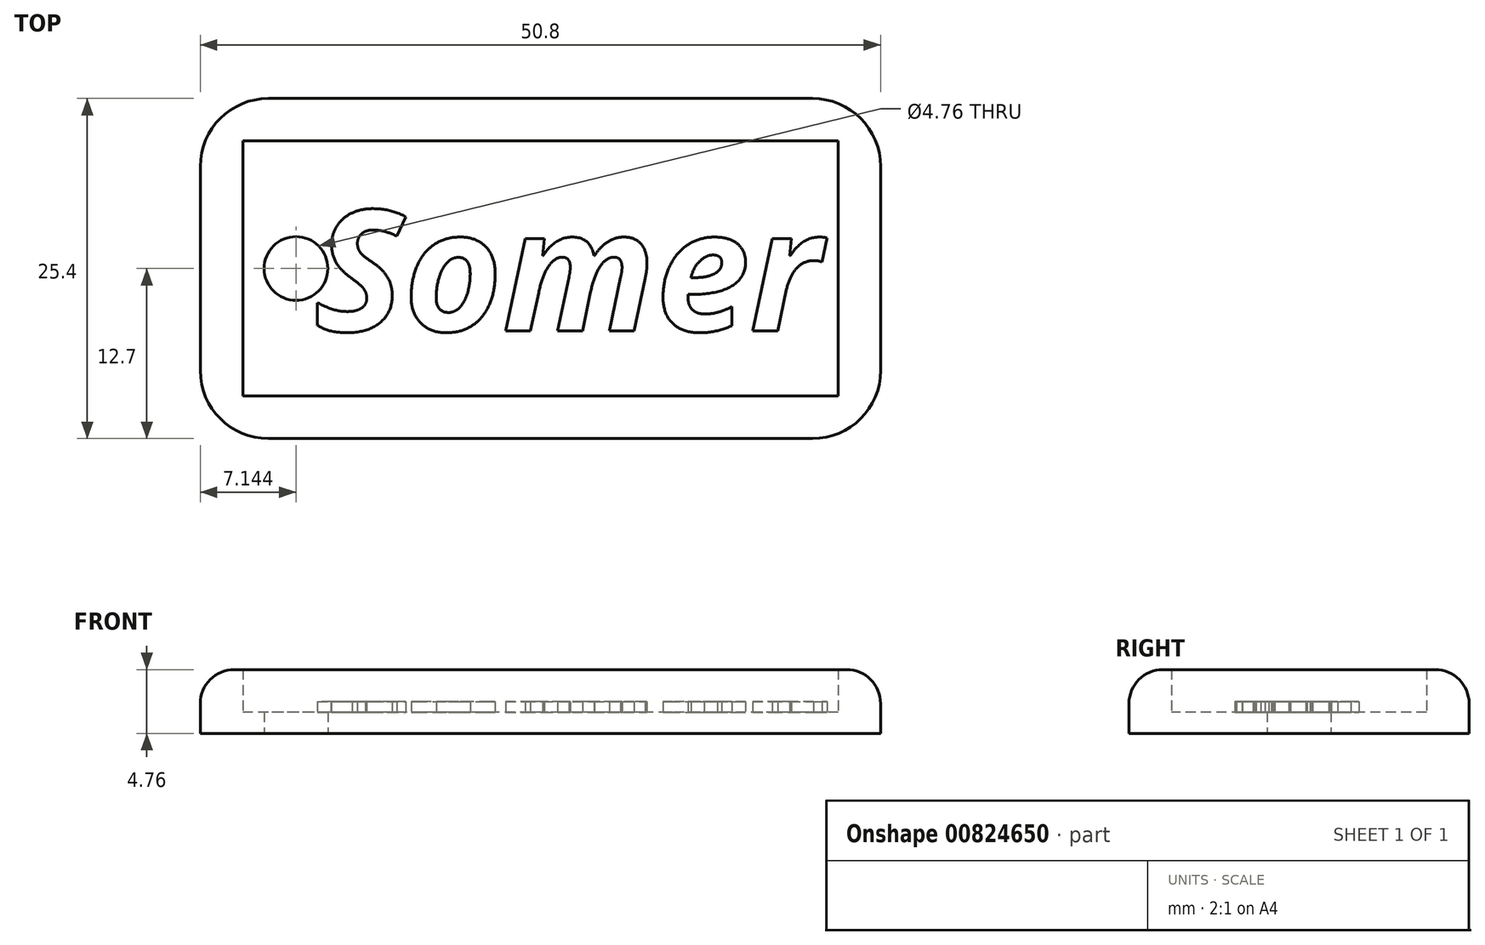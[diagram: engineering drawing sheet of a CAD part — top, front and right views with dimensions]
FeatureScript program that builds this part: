
annotation { "Feature Type Name" : "Feature", "Feature Type Description" : "" }
export const myFeature = defineFeature(function(context is Context, id is Id, definition is map)
    precondition{}
    {
        {
            var Q0;
            Q0=qCreatedBy(makeId("Top.planeOp"),FACE);
            var sketch = newSketch(context, id + "F0", { "sketchPlane" : qUnion([Q0])});
            skLineSegment(sketch, "E0.bottom", {"start": v(0, 0) * mm, "end": v(50.8, 0) * mm});
            skLineSegment(sketch, "E0.top", {"start": v(0, 25.4) * mm, "end": v(50.8, 25.4) * mm});
            skLineSegment(sketch, "E0.left", {"start": v(0, 0) * mm, "end": v(0, 25.4) * mm});
            skLineSegment(sketch, "E0.right", {"start": v(50.8, 0) * mm, "end": v(50.8, 25.4) * mm});
            skCircle(sketch, "E1", {"center": v(7.14, 12.7) * mm, "radius": 2.38 * mm});
            skPoint(sketch, "E1.centerSnap0", {"position": v(0, 12.7) * mm});
            skLineSegment(sketch, "E2.0", {"start": v(3.17, 22.23) * mm, "end": v(47.62, 22.23) * mm});
            skLineSegment(sketch, "E2.1", {"start": v(3.17, 3.18) * mm, "end": v(3.17, 22.23) * mm});
            skLineSegment(sketch, "E2.2", {"start": v(3.17, 3.18) * mm, "end": v(47.62, 3.18) * mm});
            skLineSegment(sketch, "E2.3", {"start": v(47.62, 3.18) * mm, "end": v(47.62, 22.23) * mm});
            skSolve(sketch);
        }
        {
            var Q0;
            Q0 = qSketchRegion(id + "F0", true);
            var Q1;
            Q1=makeQuery(id+"F0.imprint","IMPRINT",FACE,{"disambiguationData":[TD([[makeQuery(id+"F0.imprint","IMPRINT",EDGE,{"derivedFrom":sQuery(id+"F0.wireOp",EDGE,"E1")}),-1.0]])]});
            extrude(context, id + "F1", {"entities" : qUnion([Q0, Q1]), "depth" : 1.59 * mm, "offsetDistance" : 25.4 * mm});
        }
        {
            var Q0;
            Q0 = qSketchRegion(id + "F0", true);
            extrude(context, id + "F2", {"entities" : qUnion([Q0]), "operationType" : NewBodyOperationType.ADD, "depth" : 4.76 * mm, "offsetDistance" : 25.4 * mm});
        }
        {
            var Q0;
            {var subQ0=sQuery(id+"F0.wireOp",EDGE,"E0.right");var subQ1=sQuery(id+"F0.wireOp",EDGE,"E0.bottom");Q0=makeQuery(id+"F2.boolean.opBoolean","MERGE",EDGE,{"derivedFrom":[makeQuery(id+"F1.opExtrude","SWEPT_EDGE",EDGE,{"disambiguationData":[OSD([subQ1,subQ0])]}),makeQuery(id+"F2.opExtrude","SWEPT_EDGE",EDGE,{"disambiguationData":[OSD([subQ1,subQ0])]})]});}
            var Q1;
            {var subQ0=sQuery(id+"F0.wireOp",EDGE,"E0.left");var subQ1=sQuery(id+"F0.wireOp",EDGE,"E0.bottom");Q1=makeQuery(id+"F2.boolean.opBoolean","MERGE",EDGE,{"derivedFrom":[makeQuery(id+"F1.opExtrude","SWEPT_EDGE",EDGE,{"disambiguationData":[OSD([subQ1,subQ0])]}),makeQuery(id+"F2.opExtrude","SWEPT_EDGE",EDGE,{"disambiguationData":[OSD([subQ1,subQ0])]})]});}
            var Q2;
            {var subQ0=sQuery(id+"F0.wireOp",EDGE,"E0.right");var subQ1=sQuery(id+"F0.wireOp",EDGE,"E0.top");Q2=makeQuery(id+"F2.boolean.opBoolean","MERGE",EDGE,{"derivedFrom":[makeQuery(id+"F1.opExtrude","SWEPT_EDGE",EDGE,{"disambiguationData":[OSD([subQ1,subQ0])]}),makeQuery(id+"F2.opExtrude","SWEPT_EDGE",EDGE,{"disambiguationData":[OSD([subQ1,subQ0])]})]});}
            var Q3;
            {var subQ0=sQuery(id+"F0.wireOp",EDGE,"E0.left");var subQ1=sQuery(id+"F0.wireOp",EDGE,"E0.top");Q3=makeQuery(id+"F2.boolean.opBoolean","MERGE",EDGE,{"derivedFrom":[makeQuery(id+"F1.opExtrude","SWEPT_EDGE",EDGE,{"disambiguationData":[OSD([subQ1,subQ0])]}),makeQuery(id+"F2.opExtrude","SWEPT_EDGE",EDGE,{"disambiguationData":[OSD([subQ1,subQ0])]})]});}
            fillet(context, id + "F3", {"entities" : qUnion([Q0, Q1, Q2, Q3]), "radius" : 5.08 * mm, "tangentPropagation" : true, "allowEdgeOverflow" : false});
        }
        {
            var Q0;
            Q0=makeQuery(id+"F2.opExtrude","CAP_EDGE",EDGE,{"disambiguationData":[OSD([sQuery(id+"F0.wireOp",EDGE,"E0.bottom")])],"isStart":false});
            var Q1;
            Q1=makeQuery(id+"F2.opExtrude","CAP_EDGE",EDGE,{"disambiguationData":[OSD([sQuery(id+"F0.wireOp",EDGE,"E0.right")])],"isStart":false});
            fillet(context, id + "F4", {"entities" : qUnion([Q0, Q1]), "radius" : 2.54 * mm, "tangentPropagation" : true, "allowEdgeOverflow" : false});
        }
        {
            var Q0;
            Q0=makeQuery(id+"F1.opExtrude","CAP_FACE",FACE,{"disambiguationData":[OSD([sQuery(id+"F0.wireOp",EDGE,"E0.bottom"),sQuery(id+"F0.wireOp",EDGE,"E0.top"),sQuery(id+"F0.wireOp",EDGE,"E0.left"),sQuery(id+"F0.wireOp",EDGE,"E0.right"),sQuery(id+"F0.wireOp",EDGE,"E1")])],"isStart":false});
            var sketch = newSketch(context, id + "F5", { "sketchPlane" : qUnion([Q0])});
            skText(sketch, "E3", { "text": "Somer", "fontName": "OpenSans-BoldItalic.ttf"});
            const initialGuessF5  = {"E3": [0.0085, 0.00803, 1, 0, 0.00909]};
            skSetInitialGuess(sketch, initialGuessF5);
            skSolve(sketch);
        }
        {
            var Q0;
            Q0 = qSketchRegion(id + "F5", true);
            extrude(context, id + "F6", {"entities" : qUnion([Q0]), "operationType" : NewBodyOperationType.ADD, "depth" : 0.8 * mm, "offsetDistance" : 25.4 * mm});
        }
    });
